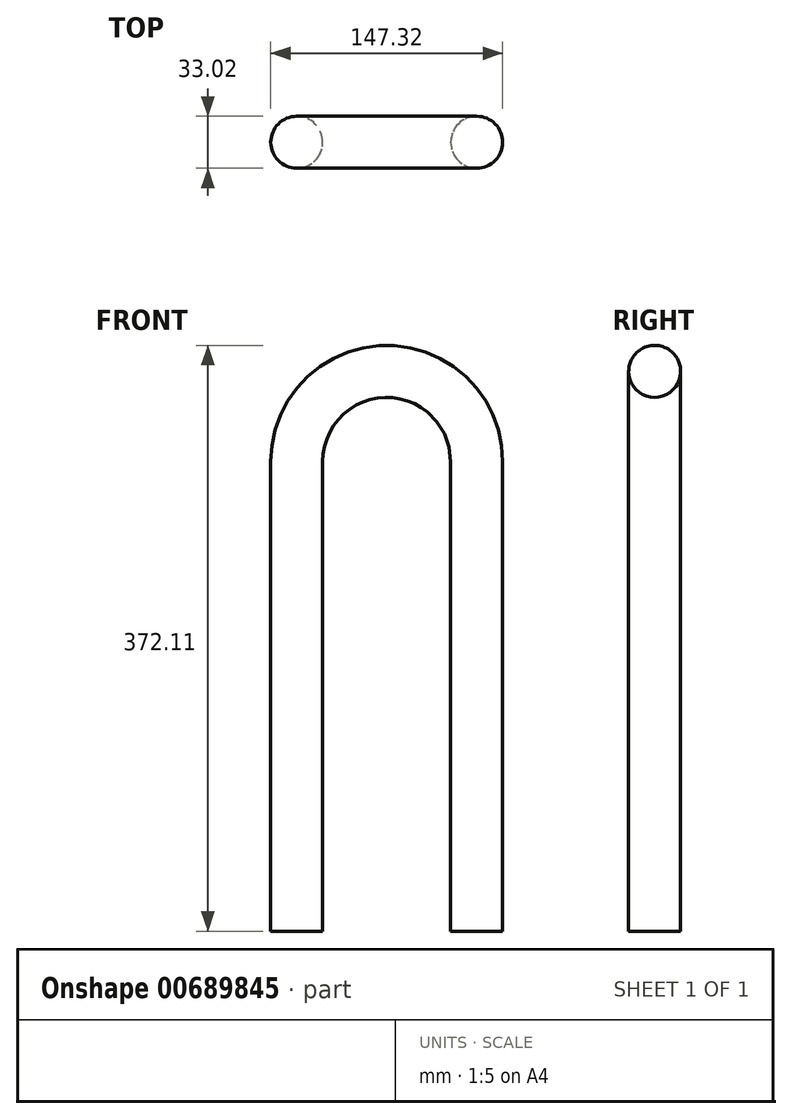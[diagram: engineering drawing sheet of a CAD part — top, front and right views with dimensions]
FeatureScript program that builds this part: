
annotation { "Feature Type Name" : "Feature", "Feature Type Description" : "" }
export const myFeature = defineFeature(function(context is Context, id is Id, definition is map)
    precondition{}
    {
        {
            var Q0;
            Q0=qCreatedBy(makeId("Front.planeOp"),FACE);
            var sketch = newSketch(context, id + "F0", { "sketchPlane" : qUnion([Q0])});
            skLineSegment(sketch, "E0.left", {"start": v(-57.15, 149.22) * mm, "end": v(-57.15, -149.23) * mm, "construction": true});
            skLineSegment(sketch, "E0.right", {"start": v(57.15, 149.23) * mm, "end": v(57.15, -149.22) * mm, "construction": true});
            skPoint(sketch, "E0.middle", {"position": v(0, 0) * mm});
            skLineSegment(sketch, "E1", {"start": v(-57.15, -149.23) * mm, "end": v(-57.15, 149.22) * mm, "construction": true});
            skLineSegment(sketch, "E2", {"start": v(57.15, -149.22) * mm, "end": v(57.15, 149.23) * mm});
            skArc(sketch, "E3", {"start": v(57.15, 149.23) * mm, "mid": v(0, 206.37) * mm, "end": v(-57.15, 149.22) * mm});
            skSolve(sketch);
        }
        {
            var Q0;
            Q0=qCreatedBy(makeId("Top.planeOp"),FACE);
            var Q1;
            Q1=sQuery(id+"F0.wireOp",VERTEX,"E0.left.end");
            cPlane(context, id + "F1", {"entities" : qUnion([Q0, Q1]), "cplaneType" : CPlaneType.PLANE_POINT, "offset" : 25.4 * mm, "width" : 152.4 * mm, "height" : 152.4 * mm});
        }
        {
            var Q0;
            Q0=qCreatedBy(id+"F1.planeOp",FACE);
            var sketch = newSketch(context, id + "F2", { "sketchPlane" : qUnion([Q0])});
            skCircle(sketch, "E4", {"center": v(57.15, 0) * mm, "radius": 16.51 * mm});
            skSolve(sketch);
        }
        {
            var Q0;
            Q0=makeQuery(id+"F2.imprint","IMPRINT",FACE,{"disambiguationData":[TD([[makeQuery(id+"F2.imprint","IMPRINT",EDGE,{"derivedFrom":sQuery(id+"F2.wireOp",EDGE,"E4")}),1.0]])]});
            var Q1;
            Q1=sQuery(id+"F0.wireOp",EDGE,"E2");
            var Q2;
            Q2=sQuery(id+"F0.wireOp",EDGE,"E3");
            sweep(context, id + "F3", {"profiles" : qUnion([Q0]), "path" : qUnion([Q1, Q2])});
        }
        {
            var Q0;
            Q0=makeQuery(id+"F3.opSweep","CAP_FACE",FACE,{"disambiguationData":[OSD([sQuery(id+"F0.wireOp",VERTEX,"E3.end"),sQuery(id+"F2.wireOp",EDGE,"E4")])],"isStart":false});
            var sketch = newSketch(context, id + "F4", { "sketchPlane" : qUnion([Q0])});
            skCircle(sketch, "E5.0", {"center": v(-57.15, 0) * mm, "radius": 16.51 * mm});
            skSolve(sketch);
        }
        {
            var Q0;
            Q0 = qSketchRegion(id + "F4", true);
            var Q1;
            Q1=makeQuery(id+"F3.opSweep","CAP_FACE",FACE,{"disambiguationData":[OSD([sQuery(id+"F0.wireOp",VERTEX,"E2.start"),sQuery(id+"F2.wireOp",EDGE,"E4")])],"isStart":true});
            extrude(context, id + "F5", {"entities" : qUnion([Q0]), "operationType" : NewBodyOperationType.ADD, "endBound" : BoundingType.UP_TO_SURFACE, "depth" : 25.4 * mm, "endBoundEntityFace" : qUnion([Q1]), "offsetDistance" : 25.4 * mm});
        }
    });
